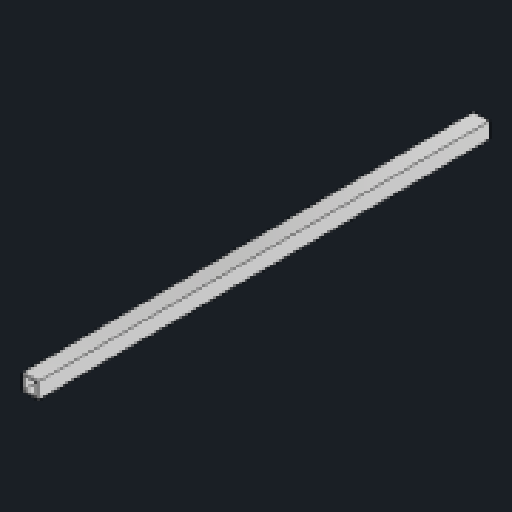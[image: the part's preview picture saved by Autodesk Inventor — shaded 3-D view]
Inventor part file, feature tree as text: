
AUTODESK INVENTOR PART (.ipt)
format: ipt  version: 2023.2 (Build 272271030, 271C)  size: 91,136 bytes
history: native  units: mm
features: extrude x1, sketch x1
ambient origin geometry x8: Origin, YZ Plane, XZ Plane, XY Plane, X Axis, Y Axis, Z Axis, Center Point
bodies: Solid1 (feature_tree)
feature tree (2):
  extrude  "Extrusion1"  Depth=0.4mm
  sketch  "Sketch1"  dims[d0=3.175mm d1=0.4mm d2=90.0mm d3=0.0mm]
